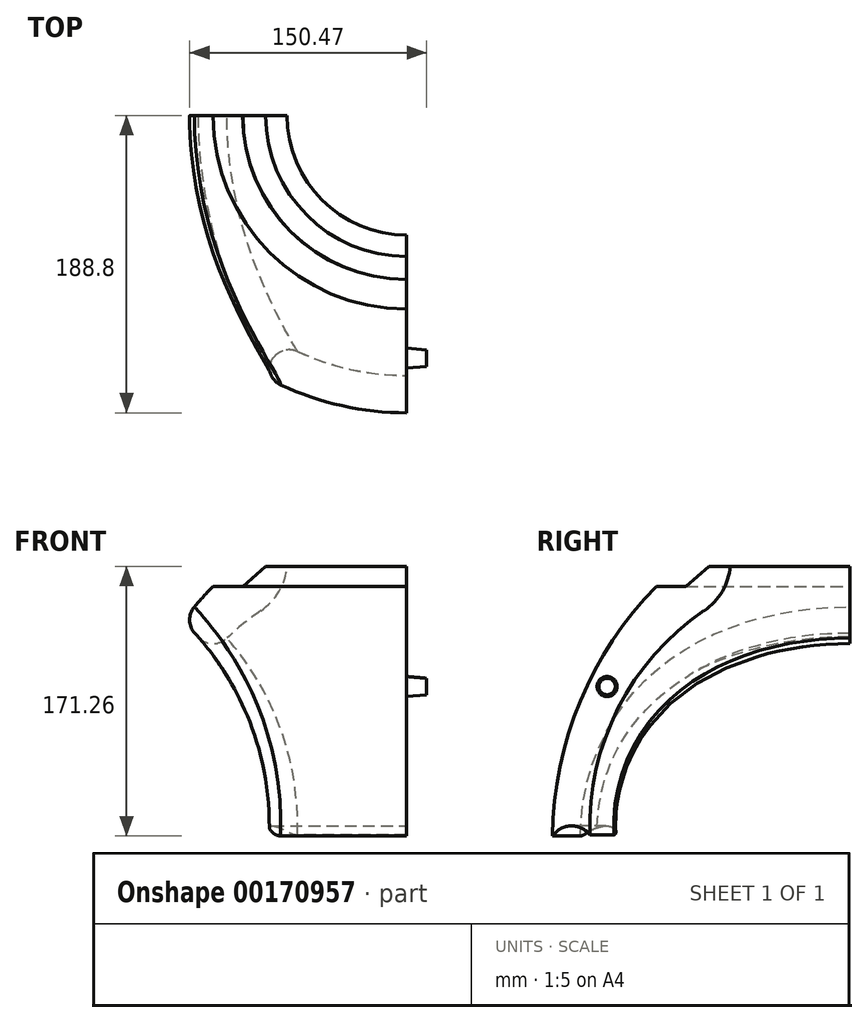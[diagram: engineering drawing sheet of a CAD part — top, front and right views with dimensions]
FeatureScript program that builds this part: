
annotation { "Feature Type Name" : "Feature", "Feature Type Description" : "" }
export const myFeature = defineFeature(function(context is Context, id is Id, definition is map)
    precondition{}
    {
        {
            var Q0;
            Q0=qCreatedBy(makeId("Front.planeOp"),FACE);
            var sketch = newSketch(context, id + "F0", { "sketchPlane" : qUnion([Q0])});
            skLineSegment(sketch, "E0", {"start": v(0, -5.54) * mm, "end": v(0, 0) * mm});
            skArc(sketch, "E1", {"start": v(-7.01, 164.95) * mm, "mid": v(-121.1, 112.22) * mm, "end": v(-165, -5.54) * mm});
            skLineSegment(sketch, "E2", {"start": v(-165, -5.54) * mm, "end": v(0, -5.54) * mm});
            skLineSegment(sketch, "E3", {"start": v(-165, -5.54) * mm, "end": v(-165, -5.54) * mm});
            skLineSegment(sketch, "E4", {"start": v(-122.9, 152.25) * mm, "end": v(-122.9, 152.25) * mm});
            skLineSegment(sketch, "E5", {"start": v(-122.9, 152.25) * mm, "end": v(-104.2, 152.25) * mm});
            skLineSegment(sketch, "E6", {"start": v(-89.51, 164.95) * mm, "end": v(-104, 152.25) * mm});
            skLineSegment(sketch, "E7", {"start": v(-104, 152.25) * mm, "end": v(-104.2, 152.25) * mm});
            skArc(sketch, "E8", {"start": v(-188.8, -6.3) * mm, "mid": v(-177.1, 0.05) * mm, "end": v(-165, -5.54) * mm});
            skArc(sketch, "E9", {"start": v(-122.9, 152.25) * mm, "mid": v(-171.13, 79.32) * mm, "end": v(-188.8, -6.3) * mm});
            skLineSegment(sketch, "E10", {"start": v(0.42, 164.95) * mm, "end": v(0, -5.54) * mm});
            skLineSegment(sketch, "E11", {"start": v(0.42, 164.95) * mm, "end": v(-89.51, 164.95) * mm});
            skSolve(sketch);
        }
        {
            var Q0;
            {var subQ2=sQuery(id+"F0.wireOp",EDGE,"E1");Q0=makeQuery(id+"F0.imprint","IMPRINT",FACE,{"disambiguationData":[TD([[makeQuery(id+"F0.imprint","IMPRINT",EDGE,{"derivedFrom":subQ2}),-1.0]])]});}
            var Q1;
            Q1=sQuery(id+"F0.wireOp",EDGE,"E0");
            revolve(context, id + "F1", {"entities" : qUnion([Q0]), "axis" : qUnion([Q1]), "revolveType" : RevolveType.ONE_DIRECTION, "angle" : 90 * degree});
        }
        {
            var Q0;
            Q0=qCreatedBy(makeId("Front.planeOp"),FACE);
            var sketch = newSketch(context, id + "F2", { "sketchPlane" : qUnion([Q0])});
            skCircle(sketch, "E12", {"center": v(-269.33, 0) * mm, "radius": 182.15 * mm});
            skSolve(sketch);
        }
        {
            var Q0;
            Q0=makeQuery(id+"F2.imprint","IMPRINT",FACE,{"disambiguationData":[TD([[makeQuery(id+"F2.imprint","IMPRINT",EDGE,{"derivedFrom":sQuery(id+"F2.wireOp",EDGE,"E12")}),1.0]])]});
            extrude(context, id + "F3", {"entities" : qUnion([Q0]), "operationType" : NewBodyOperationType.REMOVE, "endBound" : BoundingType.THROUGH_ALL, "depth" : 25.4 * mm});
        }
        {
            var Q0;
            Q0=makeQuery(id+"F3.boolean.opBoolean","INTERSECT",EDGE,{"derivedFrom":[makeQuery(id+"F1.opRevolve","SWEPT_FACE",FACE,{"disambiguationData":[OSD([sQuery(id+"F0.wireOp",EDGE,"E1")])]}),makeQuery(id+"F3.opExtrude","SWEPT_FACE",FACE,{"disambiguationData":[OSD([sQuery(id+"F2.wireOp",EDGE,"E12")])]})]});
            fillet(context, id + "F4", {"entities" : qUnion([Q0]), "radius" : 12.7 * mm, "tangentPropagation" : true, "allowEdgeOverflow" : false});
        }
        {
            var Q0;
            Q0=makeQuery(id+"F1.opRevolve","SWEPT_BODY",BODY,{"disambiguationData":[OSD([sQuery(id+"F0.wireOp",EDGE,"P5tG0YWO-6deF-1cme-UMVW-zcR6kJzPuuW9"),sQuery(id+"F0.wireOp",EDGE,"l9n6v4p5-8KPe-az1E-jcck-v7UenKci9iHe"),sQuery(id+"F0.wireOp",EDGE,"E1"),sQuery(id+"F0.wireOp",EDGE,"pzOhoHtW-SofR-Ddh6-lOb0-XZiDlA6Nqesa"),sQuery(id+"F0.wireOp",EDGE,"BmCeMnuf-rN2F-0dpX-TeqH-BNhEuHFPvOd4"),sQuery(id+"F0.wireOp",EDGE,"7X3JqiTL-AP0i-cL5I-gk5P-m7c9Aaf5Bweu")])]});
            var Q1;
            Q1=qCreatedBy(makeId("Right.planeOp"),FACE);
            mirror(context, id + "F5", {"operationType" : NewBodyOperationType.ADD, "entities" : qUnion([Q0]), "mirrorPlane" : qUnion([Q1])});
        }
        {
            var Q0;
            Q0=qCreatedBy(makeId("Front.planeOp"),FACE);
            var sketch = newSketch(context, id + "F6", { "sketchPlane" : qUnion([Q0])});
            skLineSegment(sketch, "E13.bottom", {"start": v(-110.35, 111.51) * mm, "end": v(0, 111.51) * mm});
            skLineSegment(sketch, "E13.top", {"start": v(-110.35, -19.93) * mm, "end": v(0, -19.93) * mm});
            skLineSegment(sketch, "E13.left", {"start": v(-110.35, 111.51) * mm, "end": v(-110.35, -19.93) * mm});
            skLineSegment(sketch, "E13.right", {"start": v(0, 111.51) * mm, "end": v(0, -19.93) * mm});
            skSolve(sketch);
        }
        {
            var Q0;
            Q0=qSketchRegion(id+"F6",true);
            extrude(context, id + "F7", {"entities" : qUnion([Q0]), "operationType" : NewBodyOperationType.REMOVE, "endBound" : BoundingType.THROUGH_ALL, "depth" : 25.4 * mm});
        }
        {
            var Q0;
            Q0=makeQuery(id+"F7.boolean.opBoolean","COPY",FACE,{"derivedFrom":makeQuery(id+"F7.opExtrude","SWEPT_FACE",FACE,{"disambiguationData":[OSD([sQuery(id+"F6.wireOp",EDGE,"E13.right")])]})});
            var sketch = newSketch(context, id + "F8", { "sketchPlane" : qUnion([Q0])});
            skCircle(sketch, "E14", {"center": v(154.15, 88.6) * mm, "radius": 6.35 * mm});
            skSolve(sketch);
        }
        {
            var Q0;
            Q0=qCreatedBy(makeId("Front.planeOp"),FACE);
            var sketch = newSketch(context, id + "F9", { "sketchPlane" : qUnion([Q0])});
            skLineSegment(sketch, "E15.bottom", {"start": v(-160.49, 205.4) * mm, "end": v(-2.95, 205.4) * mm});
            skLineSegment(sketch, "E15.top", {"start": v(-160.49, -21.64) * mm, "end": v(-2.95, -21.64) * mm});
            skLineSegment(sketch, "E15.left", {"start": v(-160.49, 205.4) * mm, "end": v(-160.49, -21.64) * mm});
            skLineSegment(sketch, "E15.right", {"start": v(-2.95, 205.4) * mm, "end": v(-2.95, -21.64) * mm});
            skSolve(sketch);
        }
        {
            var Q0;
            Q0=makeQuery(id+"F5.opPattern","COPY",EDGE,{"derivedFrom":makeQuery(id+"F3.boolean.opBoolean","INTERSECT",EDGE,{"derivedFrom":[makeQuery(id+"F1.opRevolve","SWEPT_FACE",FACE,{"disambiguationData":[OSD([sQuery(id+"F0.wireOp",EDGE,"E9")])]}),makeQuery(id+"F3.opExtrude","SWEPT_FACE",FACE,{"disambiguationData":[OSD([sQuery(id+"F2.wireOp",EDGE,"E12")])]})]}),"instanceName":"1"});
            fillet(context, id + "F10", {"entities" : qUnion([Q0]), "radius" : 12.7 * mm, "tangentPropagation" : true, "allowEdgeOverflow" : false});
        }
        {
            var Q0;
            Q0=qSketchRegion(id+"F9",true);
            extrude(context, id + "F11", {"entities" : qUnion([Q0]), "operationType" : NewBodyOperationType.REMOVE, "endBound" : BoundingType.THROUGH_ALL, "depth" : 25.4 * mm});
        }
        {
            var Q0;
            {var subQ0=makeQuery(id+"F1.opRevolve","SWEPT_FACE",FACE,{"disambiguationData":[OSD([sQuery(id+"F0.wireOp",EDGE,"E11")])]});Q0=makeQuery(id+"F5.boolean.opBoolean","MERGE",FACE,{"derivedFrom":[subQ0,makeQuery(id+"F5.opPattern","COPY",FACE,{"derivedFrom":subQ0,"instanceName":"1"})]});}
            var sketch = newSketch(context, id + "F12", { "sketchPlane" : qUnion([Q0])});
            skCircle(sketch, "E16", {"center": v(0, 0) * mm, "radius": 75.9 * mm});
            skSolve(sketch);
        }
        {
            var Q0;
            Q0=qSketchRegion(id+"F12",true);
            extrude(context, id + "F13", {"entities" : qUnion([Q0]), "operationType" : NewBodyOperationType.REMOVE, "endBound" : BoundingType.THROUGH_ALL, "oppositeDirection" : true, "depth" : 25.4 * mm});
        }
        {
            var Q0;
            {var subQ0=makeQuery(id+"F1.opRevolve","SWEPT_FACE",FACE,{"disambiguationData":[OSD([sQuery(id+"F0.wireOp",EDGE,"E1")])]});Q0=makeQuery(id+"F13.boolean.opBoolean","INTERSECT",EDGE,{"derivedFrom":[makeQuery(id+"F5.boolean.opBoolean","MERGE",FACE,{"derivedFrom":[subQ0,makeQuery(id+"F5.opPattern","COPY",FACE,{"derivedFrom":subQ0,"instanceName":"1"})]}),makeQuery(id+"F13.opExtrude","SWEPT_FACE",FACE,{"disambiguationData":[OSD([sQuery(id+"F12.wireOp",EDGE,"E16")])]})]});}
            fillet(context, id + "F14", {"entities" : qUnion([Q0]), "radius" : 38.1 * mm, "tangentPropagation" : true, "allowEdgeOverflow" : false});
        }
        {
            var Q0;
            Q0=makeQuery(id+"F1.opRevolve","SWEPT_BODY",BODY,{"disambiguationData":[OSD([sQuery(id+"F0.wireOp",EDGE,"E1"),sQuery(id+"F0.wireOp",EDGE,"E5"),sQuery(id+"F0.wireOp",EDGE,"E6"),sQuery(id+"F0.wireOp",EDGE,"E7"),sQuery(id+"F0.wireOp",EDGE,"E8"),sQuery(id+"F0.wireOp",EDGE,"E9"),sQuery(id+"F0.wireOp",EDGE,"E11")])]});
            var Q1;
            Q1=makeQuery(id+"F11.boolean.opBoolean","MERGE",FACE,{"derivedFrom":[makeQuery(id+"F7.boolean.opBoolean","COPY",FACE,{"derivedFrom":makeQuery(id+"F7.opExtrude","SWEPT_FACE",FACE,{"disambiguationData":[OSD([sQuery(id+"F6.wireOp",EDGE,"E13.right")])]})}),makeQuery(id+"F11.opExtrude","SWEPT_FACE",FACE,{"disambiguationData":[OSD([sQuery(id+"F9.wireOp",EDGE,"fFJiSS2h-y2lk-L0fZ-4eXj-IsiOsB7FVCmd.right")])]})]});
            mirror(context, id + "F15", {"operationType" : NewBodyOperationType.ADD, "entities" : qUnion([Q0]), "mirrorPlane" : qUnion([Q1])});
        }
        {
            var Q0;
            Q0=qCreatedBy(makeId("Front.planeOp"),FACE);
            var sketch = newSketch(context, id + "F16", { "sketchPlane" : qUnion([Q0])});
            skLineSegment(sketch, "E17.bottom", {"start": v(151.24, 196.24) * mm, "end": v(0, 196.24) * mm});
            skLineSegment(sketch, "E17.top", {"start": v(151.24, -31.23) * mm, "end": v(0, -31.23) * mm});
            skLineSegment(sketch, "E17.left", {"start": v(151.24, 196.24) * mm, "end": v(151.24, -31.23) * mm});
            skLineSegment(sketch, "E17.right", {"start": v(0, 196.24) * mm, "end": v(0, -31.23) * mm});
            skSolve(sketch);
        }
        {
            var Q0;
            Q0 = qSketchRegion(id + "F16", true);
            extrude(context, id + "F17", {"entities" : qUnion([Q0]), "operationType" : NewBodyOperationType.REMOVE, "endBound" : BoundingType.THROUGH_ALL, "depth" : 25.4 * mm});
        }
        {
            var Q0;
            Q0 = qSketchRegion(id + "F8", true);
            extrude(context, id + "F18", {"entities" : qUnion([Q0]), "operationType" : NewBodyOperationType.ADD, "oppositeDirection" : true, "depth" : 12.7 * mm, "hasDraft" : true, "draftAngle" : 5 * degree, "draftPullDirection" : true});
        }
        {
            var Q0;
            Q0=makeQuery(id+"F8.imprint","IMPRINT",FACE,{"disambiguationData":[TD([[makeQuery(id+"F8.imprint","IMPRINT",EDGE,{"derivedFrom":sQuery(id+"F8.wireOp",EDGE,"E14")}),1.0]])]});
            var Q1;
            Q1=sQuery(id+"F8.wireOp",EDGE,"E14");
            extrude(context, id + "F19", {"entities" : qUnion([Q0]), "operationType" : NewBodyOperationType.ADD, "surfaceEntities" : qUnion([Q1]), "depth" : 12.7 * mm, "hasDraft" : true, "draftAngle" : 5 * degree, "draftPullDirection" : true});
        }
    });
